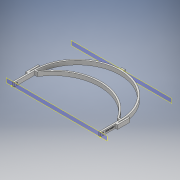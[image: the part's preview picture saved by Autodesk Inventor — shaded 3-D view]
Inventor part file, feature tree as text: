
AUTODESK INVENTOR PART (.ipt)
format: ipt  version: 2018 (Build 220112000, 112)  size: 379,392 bytes
history: native  units: mm
features: sketch x13, extrude x10, emboss x1, plane x1
ambient origin geometry x8: Origin, YZ Plane, XZ Plane, XY Plane, X Axis, Y Axis, Z Axis, Center Point
bodies: Solid1 (feature_tree)
feature tree (25):
  extrude  "Extrusion1"  Depth=200.0mm
  extrude  "Extrusion2"  Depth=45.0mm
  extrude  "Extrusion3"  Depth=3.014416mm
  emboss  "Emboss1"
  sketch  "Sketch6"  dims[d51=95.353722mm d52=93.755086mm]
  extrude  "Extrusion4"  Depth=5.0mm
  extrude  "Extrusion5"  Depth=93.755086mm
  sketch  "Sketch9"  dims[d61=85.033101mm d62=41.356791mm]
  extrude  "Extrusion6"  Depth=88.05232mm
  extrude  "Extrusion7"  Depth=105.75703mm
  extrude  "Extrusion8"  Depth=41.356791mm
  plane  "Work Plane1"
  extrude  "Extrusion9"  Depth=44.356791mm
  extrude  "Extrusion10"  Depth=41.342376mm
  sketch  "Sketch2"  dims[d33=200.0mm d34=200.0mm]
  sketch  "Sketch3"  dims[d35=45.0mm d39=45.0mm]
  sketch  "Sketch4"  dims[d44=5.0mm d45=3.014416mm]
  sketch  "Sketch5"  dims[d46=3.0mm d47=5.0mm]
  sketch  "Sketch7"  dims[d54=88.05232mm d55=17.919531mm]
  sketch  "Sketch8"  dims[d58=24.869999mm d59=105.75703mm]
  sketch  "Sketch10"  dims[d63=44.356791mm d64=44.356791mm]
  sketch  "Sketch11"  dims[d65=41.342376mm d68=105.915127mm]
  sketch  "Sketch12"  dims[d69=105.919531mm]
  sketch  "Sketch13"  dims[d70=3.0mm]
  sketch  "Sketch14"  dims[d71=20.919531mm d72=20.919531mm d73=8.0mm d74=0.0mm d79=2.0mm d80=4.0mm d81=1.674121mm d82=4.0mm d83=1.965899mm d84=6.103094mm d85=37.239096mm d86=11.769583mm d87=36.804773mm d88=6.475215mm d89=0.502994mm d90=3.0mm d91=0.0mm d92=2.0mm d93=4.0mm d94=1.447104mm d95=6.700232mm d96=3.0mm d97=0.0mm d98=1.0mm d99=0.0mm d100=4.0mm d101=3.8mm d102=2.0mm d103=1.491525mm d104=3.0mm d105=0.0mm d106=5.0mm d107=8.0mm d108=10.0mm d109=0.0mm d110=1.0mm d111=0.0mm d112=25.0mm d113=8.0mm d114=3.0mm d115=0.0mm d116=30.0mm d117=5.0mm d118=8.0mm d119=1.0mm d120=0.0mm d121=25.0mm d122=8.0mm d123=3.0mm d124=0.0mm d125=130.0mm d128=3.0mm d129=7.0mm d130=88.645483mm d131=2.0mm d132=0.0mm d133=6.969205mm d134=7.286997mm d135=98.195773mm d136=0.71276mm d137=3.0mm d138=0.0mm]
